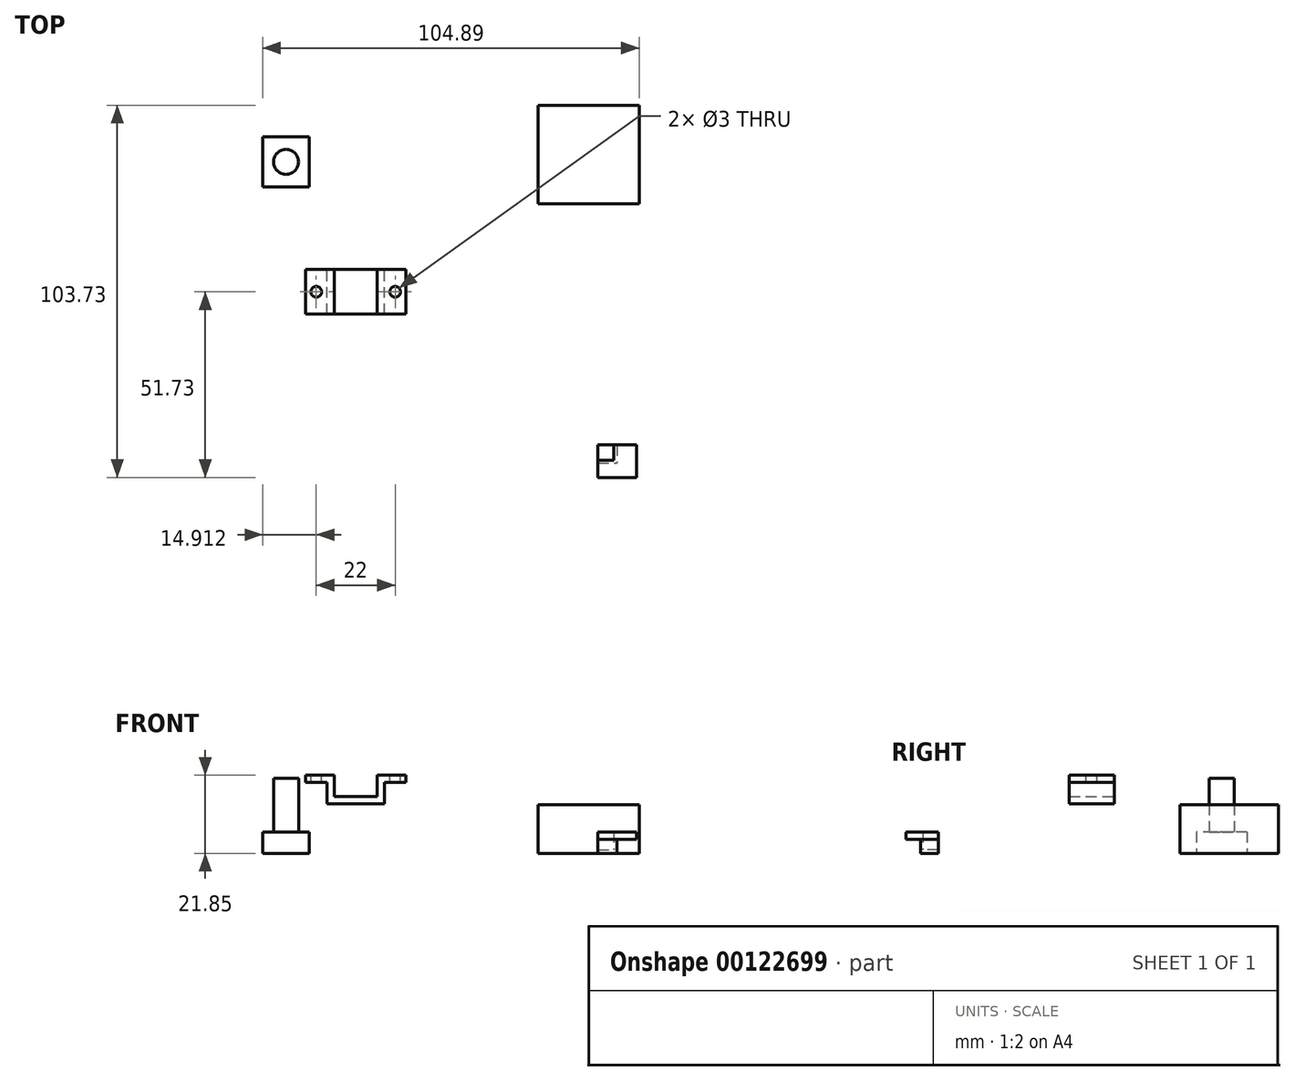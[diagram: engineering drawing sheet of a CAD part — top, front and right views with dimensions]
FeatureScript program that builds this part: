
annotation { "Feature Type Name" : "Feature", "Feature Type Description" : "" }
export const myFeature = defineFeature(function(context is Context, id is Id, definition is map)
    precondition{}
    {
        {
            var Q0;
            Q0=qCreatedBy(makeId("Front.planeOp"),FACE);
            var sketch = newSketch(context, id + "F0", { "sketchPlane" : qUnion([Q0])});
            skLineSegment(sketch, "E0", {"start": v(-31.6, 15.85) * mm, "end": v(-19.6, 15.85) * mm});
            skLineSegment(sketch, "E1", {"start": v(-19.6, 15.85) * mm, "end": v(-19.6, 21.85) * mm});
            skLineSegment(sketch, "E2", {"start": v(-19.6, 21.85) * mm, "end": v(-11.6, 21.85) * mm});
            skLineSegment(sketch, "E3", {"start": v(-11.6, 21.85) * mm, "end": v(-11.6, 19.85) * mm});
            skLineSegment(sketch, "E4", {"start": v(-11.6, 19.85) * mm, "end": v(-17.6, 19.85) * mm});
            skLineSegment(sketch, "E5", {"start": v(-17.6, 19.85) * mm, "end": v(-17.6, 13.85) * mm});
            skLineSegment(sketch, "E6", {"start": v(-17.6, 13.85) * mm, "end": v(-33.6, 13.85) * mm});
            skLineSegment(sketch, "E7", {"start": v(-33.6, 13.85) * mm, "end": v(-33.6, 19.85) * mm});
            skLineSegment(sketch, "E8", {"start": v(-33.6, 19.85) * mm, "end": v(-39.6, 19.85) * mm});
            skLineSegment(sketch, "E9", {"start": v(-39.6, 19.85) * mm, "end": v(-39.6, 21.85) * mm});
            skLineSegment(sketch, "E10", {"start": v(-39.6, 21.85) * mm, "end": v(-31.6, 21.85) * mm});
            skLineSegment(sketch, "E11", {"start": v(-31.6, 21.85) * mm, "end": v(-31.6, 15.85) * mm});
            skSolve(sketch);
        }
        {
            var Q0;
            Q0=qSketchRegion(id+"F0",true);
            extrude(context, id + "F1", {"entities" : qUnion([Q0]), "depth" : 12.5 * mm});
        }
        {
            var Q0;
            Q0=makeQuery(id+"F1.opExtrude","CAP_FACE",FACE,{"disambiguationData":[OSD([sQuery(id+"F0.wireOp",EDGE,"E0"),sQuery(id+"F0.wireOp",EDGE,"E1"),sQuery(id+"F0.wireOp",EDGE,"E2"),sQuery(id+"F0.wireOp",EDGE,"E3"),sQuery(id+"F0.wireOp",EDGE,"E4"),sQuery(id+"F0.wireOp",EDGE,"E5"),sQuery(id+"F0.wireOp",EDGE,"E6"),sQuery(id+"F0.wireOp",EDGE,"E7"),sQuery(id+"F0.wireOp",EDGE,"E8"),sQuery(id+"F0.wireOp",EDGE,"E9"),sQuery(id+"F0.wireOp",EDGE,"E10"),sQuery(id+"F0.wireOp",EDGE,"E11")])],"isStart":false});
            cPlane(context, id + "F2", {"entities" : qUnion([Q0]), "cplaneType" : CPlaneType.OFFSET, "offset" : 2 * mm, "width" : 150 * mm, "height" : 150 * mm});
        }
        {
            var Q0;
            Q0=makeQuery(id+"F1.opExtrude","SWEPT_FACE",FACE,{"disambiguationData":[OSD([sQuery(id+"F0.wireOp",EDGE,"E10")])]});
            var sketch = newSketch(context, id + "F3", { "sketchPlane" : qUnion([Q0])});
            skCircle(sketch, "E12", {"center": v(-36.6, -6.25) * mm, "radius": 1.5 * mm});
            skCircle(sketch, "E13", {"center": v(-14.6, -6.25) * mm, "radius": 1.5 * mm});
            skSolve(sketch);
        }
        {
            var Q0;
            Q0=qSketchRegion(id+"F3",true);
            extrude(context, id + "F4", {"entities" : qUnion([Q0]), "operationType" : NewBodyOperationType.REMOVE, "oppositeDirection" : true, "depth" : 2 * mm});
        }
        {
            var Q0;
            Q0=qCreatedBy(makeId("Top.planeOp"),FACE);
            var sketch = newSketch(context, id + "F5", { "sketchPlane" : qUnion([Q0])});
            skLineSegment(sketch, "E14.bottom", {"start": v(-51.52, 36.97) * mm, "end": v(-38.52, 36.97) * mm});
            skLineSegment(sketch, "E14.top", {"start": v(-51.52, 22.97) * mm, "end": v(-38.52, 22.97) * mm});
            skLineSegment(sketch, "E14.left", {"start": v(-51.52, 36.97) * mm, "end": v(-51.52, 22.97) * mm});
            skLineSegment(sketch, "E14.right", {"start": v(-38.52, 36.97) * mm, "end": v(-38.52, 22.97) * mm});
            skSolve(sketch);
        }
        {
            var Q0;
            Q0=qSketchRegion(id+"F5",true);
            extrude(context, id + "F6", {"entities" : qUnion([Q0]), "depth" : 6 * mm});
        }
        {
            var Q0;
            Q0=makeQuery(id+"F6.opExtrude","CAP_FACE",FACE,{"disambiguationData":[OSD([sQuery(id+"F5.wireOp",EDGE,"E14.bottom"),sQuery(id+"F5.wireOp",EDGE,"E14.top"),sQuery(id+"F5.wireOp",EDGE,"E14.left"),sQuery(id+"F5.wireOp",EDGE,"E14.right")])],"isStart":false});
            var sketch = newSketch(context, id + "F7", { "sketchPlane" : qUnion([Q0])});
            skCircle(sketch, "E15", {"center": v(-45.02, 29.97) * mm, "radius": 3.5 * mm});
            skSolve(sketch);
        }
        {
            var Q0;
            Q0=qSketchRegion(id+"F7",true);
            extrude(context, id + "F8", {"entities" : qUnion([Q0]), "operationType" : NewBodyOperationType.ADD, "depth" : 15 * mm});
        }
        {
            var Q0;
            Q0=qCreatedBy(makeId("Top.planeOp"),FACE);
            var sketch = newSketch(context, id + "F9", { "sketchPlane" : qUnion([Q0])});
            skLineSegment(sketch, "E16.bottom", {"start": v(41.85, -48.95) * mm, "end": v(47.23, -48.95) * mm});
            skLineSegment(sketch, "E16.top", {"start": v(41.85, -53.96) * mm, "end": v(47.23, -53.96) * mm});
            skLineSegment(sketch, "E16.left", {"start": v(41.85, -48.95) * mm, "end": v(41.85, -53.96) * mm});
            skLineSegment(sketch, "E16.right", {"start": v(47.23, -48.95) * mm, "end": v(47.23, -53.96) * mm});
            skSolve(sketch);
        }
        {
            var Q0;
            Q0=qSketchRegion(id+"F9",true);
            extrude(context, id + "F10", {"entities" : qUnion([Q0]), "depth" : 1 * mm});
        }
        {
            var Q0;
            Q0=makeQuery(id+"F10.opExtrude","CAP_FACE",FACE,{"disambiguationData":[OSD([sQuery(id+"F9.wireOp",EDGE,"E16.bottom"),sQuery(id+"F9.wireOp",EDGE,"E16.top"),sQuery(id+"F9.wireOp",EDGE,"E16.left"),sQuery(id+"F9.wireOp",EDGE,"E16.right")])],"isStart":false});
            var sketch = newSketch(context, id + "F11", { "sketchPlane" : qUnion([Q0])});
            skLineSegment(sketch, "E17.bottom", {"start": v(46.24, -48.95) * mm, "end": v(47.23, -48.95) * mm});
            skLineSegment(sketch, "E17.top", {"start": v(41.85, -53.96) * mm, "end": v(47.23, -53.96) * mm});
            skLineSegment(sketch, "E17.left", {"start": v(41.85, -53.28) * mm, "end": v(41.85, -53.96) * mm});
            skLineSegment(sketch, "E17.right", {"start": v(47.23, -48.95) * mm, "end": v(47.23, -53.96) * mm});
            skLineSegment(sketch, "E18.top", {"start": v(41.85, -53.28) * mm, "end": v(46.24, -53.28) * mm});
            skLineSegment(sketch, "E18.right", {"start": v(46.24, -48.95) * mm, "end": v(46.24, -53.28) * mm});
            skSolve(sketch);
        }
        {
            var Q0;
            Q0=qSketchRegion(id+"F11",true);
            extrude(context, id + "F12", {"entities" : qUnion([Q0]), "operationType" : NewBodyOperationType.ADD, "depth" : 5 * mm});
        }
        {
            var Q0;
            Q0=makeQuery(id+"F12.opExtrude","CAP_FACE",FACE,{"disambiguationData":[OSD([sQuery(id+"F11.wireOp",EDGE,"E17.bottom"),sQuery(id+"F11.wireOp",EDGE,"E17.top"),sQuery(id+"F11.wireOp",EDGE,"E17.left"),sQuery(id+"F11.wireOp",EDGE,"E17.right"),sQuery(id+"F11.wireOp",EDGE,"E18.top"),sQuery(id+"F11.wireOp",EDGE,"E18.right")])],"isStart":false});
            cPlane(context, id + "F13", {"entities" : qUnion([Q0]), "cplaneType" : CPlaneType.OFFSET, "offset" : 2 * mm, "oppositeDirection" : true, "width" : 150 * mm, "height" : 150 * mm});
        }
        {
            var Q0;
            Q0=qCreatedBy(id+"F13.planeOp",FACE);
            var sketch = newSketch(context, id + "F14", { "sketchPlane" : qUnion([Q0])});
            skLineSegment(sketch, "E19.bottom", {"start": v(47.23, -48.95) * mm, "end": v(52.67, -48.95) * mm});
            skLineSegment(sketch, "E19.top", {"start": v(41.85, -57.98) * mm, "end": v(52.67, -57.98) * mm});
            skLineSegment(sketch, "E19.left", {"start": v(41.85, -53.96) * mm, "end": v(41.85, -57.98) * mm});
            skLineSegment(sketch, "E19.right", {"start": v(52.67, -48.95) * mm, "end": v(52.67, -57.98) * mm});
            skLineSegment(sketch, "E20.top", {"start": v(41.85, -53.96) * mm, "end": v(47.23, -53.96) * mm});
            skLineSegment(sketch, "E20.right", {"start": v(47.23, -48.95) * mm, "end": v(47.23, -53.96) * mm});
            skSolve(sketch);
        }
        {
            var Q0;
            Q0=qSketchRegion(id+"F14",true);
            extrude(context, id + "F15", {"entities" : qUnion([Q0]), "operationType" : NewBodyOperationType.ADD, "depth" : 2 * mm});
        }
        {
            var Q0;
            Q0=qCreatedBy(makeId("Top.planeOp"),FACE);
            var sketch = newSketch(context, id + "F16", { "sketchPlane" : qUnion([Q0])});
            skLineSegment(sketch, "E21.bottom", {"start": v(25.13, 45.75) * mm, "end": v(53.37, 45.75) * mm});
            skLineSegment(sketch, "E21.top", {"start": v(25.13, 18.3) * mm, "end": v(53.37, 18.3) * mm});
            skLineSegment(sketch, "E21.left", {"start": v(25.13, 45.75) * mm, "end": v(25.13, 18.3) * mm});
            skLineSegment(sketch, "E21.right", {"start": v(53.37, 45.75) * mm, "end": v(53.37, 18.3) * mm});
            skSolve(sketch);
        }
        {
            var Q0;
            Q0=qSketchRegion(id+"F16",true);
            extrude(context, id + "F17", {"entities" : qUnion([Q0]), "depth" : 13.66 * mm});
        }
    });
